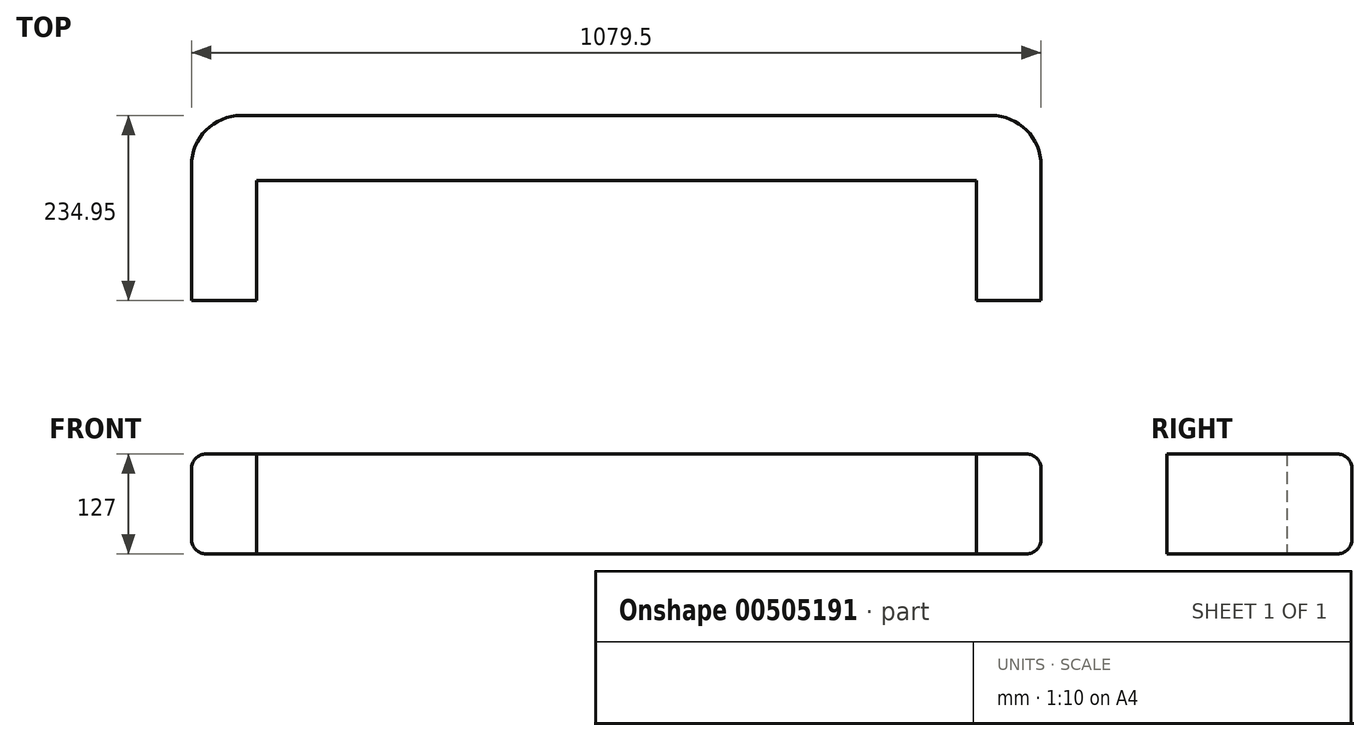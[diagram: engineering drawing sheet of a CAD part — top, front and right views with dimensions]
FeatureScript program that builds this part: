
annotation { "Feature Type Name" : "Feature", "Feature Type Description" : "" }
export const myFeature = defineFeature(function(context is Context, id is Id, definition is map)
    precondition{}
    {
        {
            var Q0;
            Q0=qCreatedBy(makeId("Front.planeOp"),FACE);
            var sketch = newSketch(context, id + "F0", { "sketchPlane" : qUnion([Q0])});
            skLineSegment(sketch, "E0.bottom", {"start": v(-41.93, 90.93) * mm, "end": v(872.47, 90.93) * mm});
            skLineSegment(sketch, "E0.top", {"start": v(-41.93, -36.07) * mm, "end": v(872.47, -36.07) * mm});
            skLineSegment(sketch, "E0.left", {"start": v(-41.93, 90.93) * mm, "end": v(-41.93, -36.07) * mm});
            skLineSegment(sketch, "E0.right", {"start": v(872.47, 90.93) * mm, "end": v(872.47, -36.07) * mm});
            skSolve(sketch);
        }
        {
            var Q0;
            Q0=qSketchRegion(id+"F0",true);
            extrude(context, id + "F1", {"entities" : qUnion([Q0]), "depth" : 19.05 * mm});
        }
        {
            var Q0;
            Q0=makeQuery(id+"F1.opExtrude","SWEPT_FACE",FACE,{"disambiguationData":[OSD([sQuery(id+"F0.wireOp",EDGE,"E0.left")])]});
            var sketch = newSketch(context, id + "F2", { "sketchPlane" : qUnion([Q0])});
            skLineSegment(sketch, "E1.bottom", {"start": v(0, 90.93) * mm, "end": v(171.45, 90.93) * mm});
            skLineSegment(sketch, "E1.top", {"start": v(0, -36.07) * mm, "end": v(171.45, -36.07) * mm});
            skLineSegment(sketch, "E1.left", {"start": v(0, 90.93) * mm, "end": v(0, -36.07) * mm});
            skLineSegment(sketch, "E1.right", {"start": v(171.45, 90.93) * mm, "end": v(171.45, -36.07) * mm});
            skSolve(sketch);
        }
        {
            var Q0;
            Q0=qSketchRegion(id+"F2",true);
            extrude(context, id + "F3", {"entities" : qUnion([Q0]), "operationType" : NewBodyOperationType.ADD, "depth" : 19.05 * mm});
        }
        {
            var Q0;
            Q0=makeQuery(id+"F1.opExtrude","SWEPT_FACE",FACE,{"disambiguationData":[OSD([sQuery(id+"F0.wireOp",EDGE,"E0.right")])]});
            var sketch = newSketch(context, id + "F4", { "sketchPlane" : qUnion([Q0])});
            skLineSegment(sketch, "E2.bottom", {"start": v(0, 90.93) * mm, "end": v(-171.45, 90.93) * mm});
            skLineSegment(sketch, "E2.top", {"start": v(0, -36.07) * mm, "end": v(-171.45, -36.07) * mm});
            skLineSegment(sketch, "E2.left", {"start": v(0, 90.93) * mm, "end": v(0, -36.07) * mm});
            skLineSegment(sketch, "E2.right", {"start": v(-171.45, 90.93) * mm, "end": v(-171.45, -36.07) * mm});
            skSolve(sketch);
        }
        {
            var Q0;
            Q0=qSketchRegion(id+"F4",true);
            extrude(context, id + "F5", {"entities" : qUnion([Q0]), "operationType" : NewBodyOperationType.ADD, "depth" : 19.05 * mm});
        }
        {
            var Q0;
            Q0=qCreatedBy(makeId("Front.planeOp"),FACE);
            var sketch = newSketch(context, id + "F6", { "sketchPlane" : qUnion([Q0])});
            skLineSegment(sketch, "E3.bottom", {"start": v(-105.43, 90.93) * mm, "end": v(-60.98, 90.93) * mm});
            skLineSegment(sketch, "E3.top", {"start": v(-105.43, -36.07) * mm, "end": v(-60.98, -36.07) * mm});
            skLineSegment(sketch, "E3.left", {"start": v(-124.48, 71.88) * mm, "end": v(-124.48, -17.02) * mm});
            skLineSegment(sketch, "E3.right", {"start": v(-60.98, 90.93) * mm, "end": v(-60.98, -36.07) * mm});
            skPoint(sketch, "E4.visualSharp", {"position": v(-124.48, -36.07) * mm});
            skArc(sketch, "E4.filletArc", {"start": v(-124.48, -17.02) * mm, "mid": v(-118.9, -30.49) * mm, "end": v(-105.43, -36.07) * mm});
            skPoint(sketch, "E5.visualSharp", {"position": v(-124.48, 90.93) * mm});
            skArc(sketch, "E5.filletArc", {"start": v(-105.43, 90.93) * mm, "mid": v(-118.9, 85.35) * mm, "end": v(-124.48, 71.88) * mm});
            skSolve(sketch);
        }
        {
            var Q0;
            Q0=qSketchRegion(id+"F6",true);
            extrude(context, id + "F7", {"entities" : qUnion([Q0]), "operationType" : NewBodyOperationType.ADD, "depth" : 171.45 * mm});
        }
        {
            var Q0;
            Q0=qSketchRegion(id+"F6",true);
            var Q1;
            Q1=sQuery(id+"F6.wireOp",EDGE,"E3.right");
            revolve(context, id + "F8", {"operationType" : NewBodyOperationType.ADD, "entities" : qUnion([Q0]), "axis" : qUnion([Q1]), "revolveType" : RevolveType.ONE_DIRECTION, "angle" : 90 * degree});
        }
        {
            var Q0;
            Q0=makeQuery(id+"F8.opRevolve","CAP_FACE",FACE,{"disambiguationData":[OSD([sQuery(id+"F6.wireOp",EDGE,"E3.bottom"),sQuery(id+"F6.wireOp",EDGE,"E3.top"),sQuery(id+"F6.wireOp",EDGE,"E3.left"),sQuery(id+"F6.wireOp",EDGE,"E3.right"),sQuery(id+"F6.wireOp",EDGE,"E4.filletArc"),sQuery(id+"F6.wireOp",EDGE,"E5.filletArc")])],"isStart":false});
            var sketch = newSketch(context, id + "F9", { "sketchPlane" : qUnion([Q0])});
            skLineSegment(sketch, "E6.bottom", {"start": v(0, 90.93) * mm, "end": v(63.5, 90.93) * mm});
            skLineSegment(sketch, "E6.top", {"start": v(0, -36.07) * mm, "end": v(63.5, -36.07) * mm});
            skLineSegment(sketch, "E6.left", {"start": v(0, 90.93) * mm, "end": v(0, -36.07) * mm});
            skLineSegment(sketch, "E6.right", {"start": v(63.5, 90.93) * mm, "end": v(63.5, -36.07) * mm});
            skSolve(sketch);
        }
        {
            var Q0;
            Q0=qSketchRegion(id+"F9",true);
            extrude(context, id + "F10", {"entities" : qUnion([Q0]), "operationType" : NewBodyOperationType.ADD, "depth" : 952.5 * mm});
        }
        {
            var Q0;
            Q0=makeQuery(id+"F10.opExtrude","SWEPT_EDGE",EDGE,{"disambiguationData":[OSD([sQuery(id+"F9.wireOp",EDGE,"E6.bottom"),sQuery(id+"F9.wireOp",EDGE,"E6.right")])]});
            var Q1;
            Q1=makeQuery(id+"F10.opExtrude","SWEPT_EDGE",EDGE,{"disambiguationData":[OSD([sQuery(id+"F9.wireOp",EDGE,"E6.top"),sQuery(id+"F9.wireOp",EDGE,"E6.right")])]});
            fillet(context, id + "F11", {"entities" : qUnion([Q0, Q1]), "radius" : 19.05 * mm, "tangentPropagation" : true, "allowEdgeOverflow" : false});
        }
        {
            var Q0;
            Q0=makeQuery(id+"F10.boolean.opBoolean","MERGE",FACE,{"derivedFrom":[makeQuery(id+"F5.opExtrude","CAP_FACE",FACE,{"disambiguationData":[OSD([sQuery(id+"F4.wireOp",EDGE,"E2.bottom"),sQuery(id+"F4.wireOp",EDGE,"E2.top"),sQuery(id+"F4.wireOp",EDGE,"E2.left"),sQuery(id+"F4.wireOp",EDGE,"E2.right")])],"isStart":false}),makeQuery(id+"F10.opExtrude","CAP_FACE",FACE,{"disambiguationData":[OSD([sQuery(id+"F9.wireOp",EDGE,"E6.bottom"),sQuery(id+"F9.wireOp",EDGE,"E6.top"),sQuery(id+"F9.wireOp",EDGE,"E6.left"),sQuery(id+"F9.wireOp",EDGE,"E6.right")])],"isStart":false})]});
            var sketch = newSketch(context, id + "F12", { "sketchPlane" : qUnion([Q0])});
            skLineSegment(sketch, "E7.bottom", {"start": v(0, -36.07) * mm, "end": v(63.5, -36.07) * mm});
            skLineSegment(sketch, "E7.top", {"start": v(0, 90.93) * mm, "end": v(63.5, 90.93) * mm});
            skLineSegment(sketch, "E7.left", {"start": v(0, -36.07) * mm, "end": v(0, 90.93) * mm});
            skLineSegment(sketch, "E7.right", {"start": v(63.5, -36.07) * mm, "end": v(63.5, 90.93) * mm});
            skSolve(sketch);
        }
        {
            var Q0;
            Q0=qSketchRegion(id+"F12",true);
            var Q1;
            Q1=sQuery(id+"F12.wireOp",EDGE,"E7.left");
            revolve(context, id + "F13", {"operationType" : NewBodyOperationType.ADD, "entities" : qUnion([Q0]), "axis" : qUnion([Q1]), "revolveType" : RevolveType.ONE_DIRECTION, "oppositeDirection" : true, "angle" : 90 * degree});
        }
        {
            var Q0;
            Q0=makeQuery(id+"F13.opRevolve","SWEPT_EDGE",EDGE,{"disambiguationData":[OSD([sQuery(id+"F12.wireOp",EDGE,"E7.top"),sQuery(id+"F12.wireOp",EDGE,"E7.right")])]});
            var Q1;
            Q1=makeQuery(id+"F13.opRevolve","SWEPT_EDGE",EDGE,{"disambiguationData":[OSD([sQuery(id+"F12.wireOp",EDGE,"E7.bottom"),sQuery(id+"F12.wireOp",EDGE,"E7.right")])]});
            fillet(context, id + "F14", {"entities" : qUnion([Q0, Q1]), "radius" : 19.05 * mm, "tangentPropagation" : true, "allowEdgeOverflow" : false});
        }
        {
            var Q0;
            Q0=makeQuery(id+"F13.opRevolve","CAP_FACE",FACE,{"disambiguationData":[OSD([sQuery(id+"F12.wireOp",EDGE,"E7.bottom"),sQuery(id+"F12.wireOp",EDGE,"E7.top"),sQuery(id+"F12.wireOp",EDGE,"E7.left"),sQuery(id+"F12.wireOp",EDGE,"E7.right")])],"isStart":false});
            var sketch = newSketch(context, id + "F15", { "sketchPlane" : qUnion([Q0])});
            skLineSegment(sketch, "E8.bottom", {"start": v(891.52, -36.07) * mm, "end": v(955.02, -36.07) * mm});
            skLineSegment(sketch, "E8.top", {"start": v(891.52, 90.93) * mm, "end": v(955.02, 90.93) * mm});
            skLineSegment(sketch, "E8.left", {"start": v(891.52, -36.07) * mm, "end": v(891.52, 90.93) * mm});
            skLineSegment(sketch, "E8.right", {"start": v(955.02, -36.07) * mm, "end": v(955.02, 90.93) * mm});
            skSolve(sketch);
        }
        {
            var Q0;
            Q0=qSketchRegion(id+"F15",true);
            extrude(context, id + "F16", {"entities" : qUnion([Q0]), "operationType" : NewBodyOperationType.ADD, "depth" : 171.45 * mm});
        }
        {
            var Q0;
            Q0=makeQuery(id+"F16.opExtrude","SWEPT_EDGE",EDGE,{"disambiguationData":[OSD([sQuery(id+"F15.wireOp",EDGE,"E8.top"),sQuery(id+"F15.wireOp",EDGE,"E8.right")])]});
            var Q1;
            Q1=makeQuery(id+"F16.opExtrude","SWEPT_EDGE",EDGE,{"disambiguationData":[OSD([sQuery(id+"F15.wireOp",EDGE,"E8.bottom"),sQuery(id+"F15.wireOp",EDGE,"E8.right")])]});
            fillet(context, id + "F17", {"entities" : qUnion([Q0, Q1]), "radius" : 19.05 * mm, "tangentPropagation" : true, "allowEdgeOverflow" : false});
        }
    });
